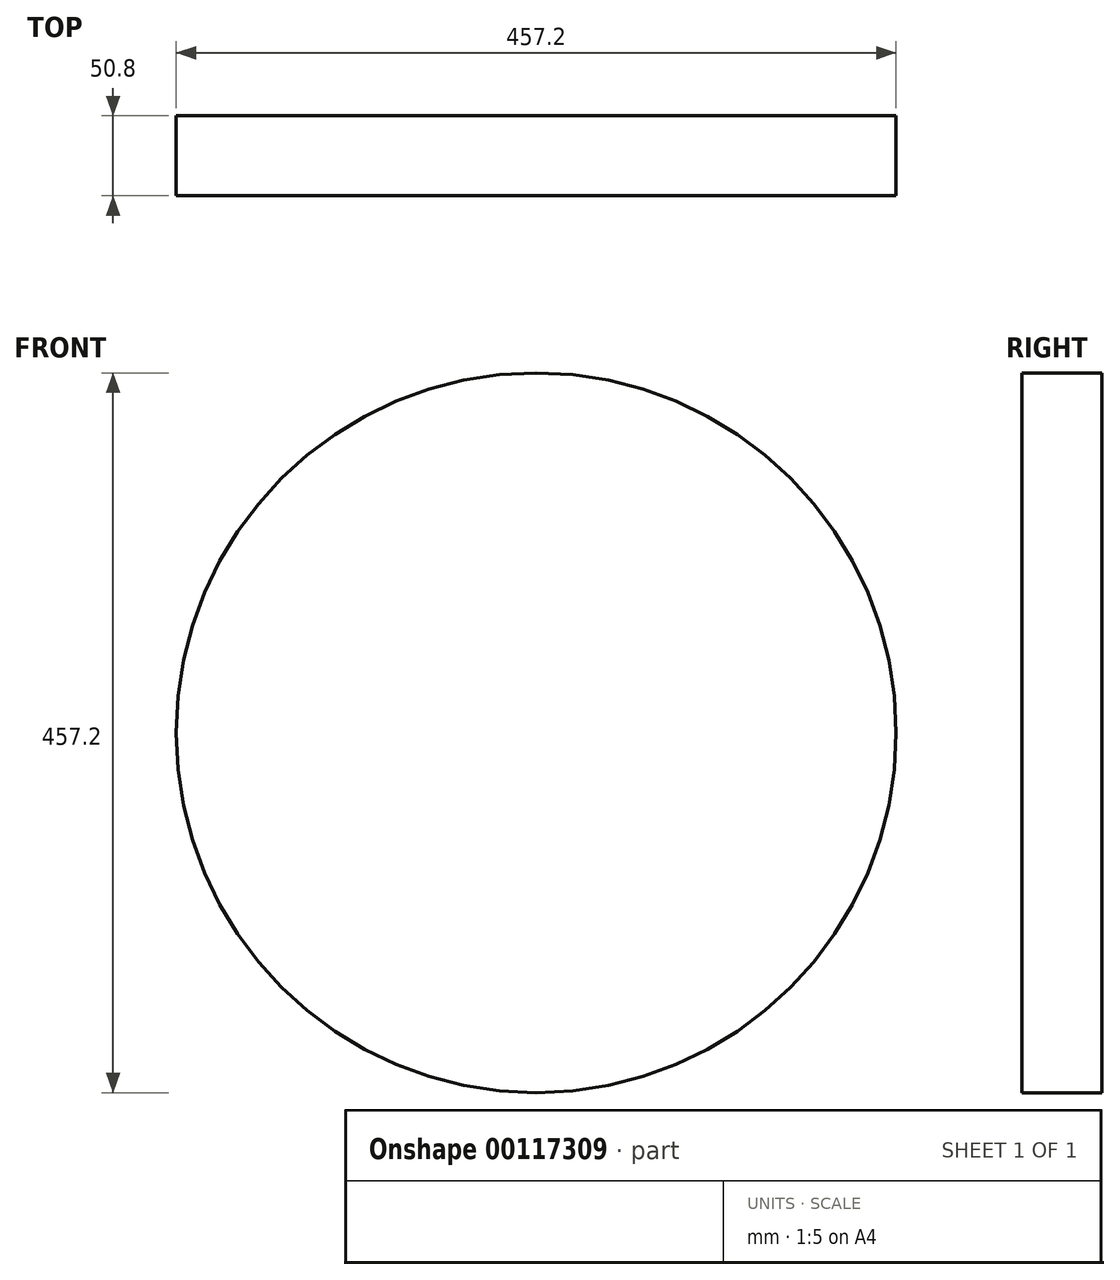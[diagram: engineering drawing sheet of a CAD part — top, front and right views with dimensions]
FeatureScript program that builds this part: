
annotation { "Feature Type Name" : "Feature", "Feature Type Description" : "" }
export const myFeature = defineFeature(function(context is Context, id is Id, definition is map)
    precondition{}
    {
        {
            var Q0;
            Q0=qCreatedBy(makeId("Front.planeOp"),FACE);
            var sketch = newSketch(context, id + "F0", { "sketchPlane" : qUnion([Q0])});
            skCircle(sketch, "E0", {"center": v(-94.2, 46.25) * mm, "radius": 228.6 * mm});
            skSolve(sketch);
        }
        {
            var Q0;
            Q0=makeQuery(id+"F0.imprint","IMPRINT",FACE,{"disambiguationData":[TD([[makeQuery(id+"F0.imprint","IMPRINT",EDGE,{"derivedFrom":sQuery(id+"F0.wireOp",EDGE,"E0")}),1.0]])]});
            var Q1;
            Q1=sQuery(id+"F0.wireOp",EDGE,"E0");
            extrude(context, id + "F1", {"entities" : qUnion([Q0]), "bodyType" : ToolBodyType.SURFACE, "surfaceEntities" : qUnion([Q1]), "depth" : 50.8 * mm});
        }
    });
